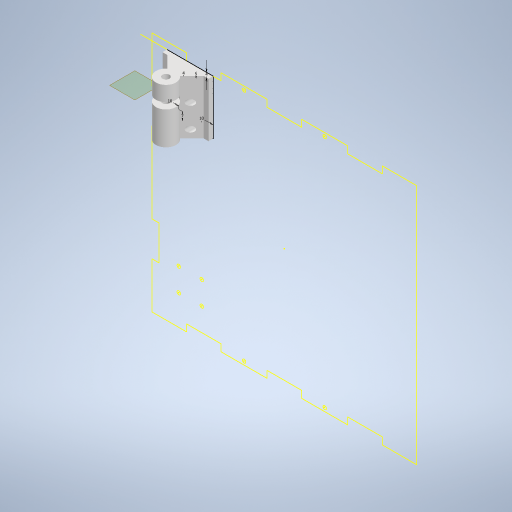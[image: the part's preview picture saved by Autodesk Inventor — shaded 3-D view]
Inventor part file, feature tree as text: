
AUTODESK INVENTOR PART (.ipt)
format: ipt  version: 2024.2 (Build 282272000, 272)  size: 331,776 bytes
history: native  units: mm
features: other x6, extrude x5, sketch x4, reference x3, chamfer x2
ambient origin geometry x8: Origin, YZ Plane, XZ Plane, XY Plane, X Axis, Y Axis, Z Axis, Center Point
bodies: Body1 (feature_tree)
feature tree (20):
  other  "Твердое тело1"
  sketch  "Эскиз1"
  extrude  "Выдавливание1"  Depth=10.0mm
  other  "РабПлоскость1"
  extrude  "Выдавливание3"  Depth=10.0mm
  extrude  "Выдавливание4"  Depth=7.0mm
  chamfer  "Фаска3"  Distance=4.0mm
  chamfer  "Фаска4"  Distance=5.0mm
  extrude  "Выдавливание5"  Depth=4.0mm
  extrude  "Выдавливание6"  Depth=4.0mm TaperAngle=0.0deg
  reference  "Ссылка1"
  reference  "Ссылка2"
  reference  "Ссылка3"
  sketch  "Эскиз2"
  sketch  "Эскиз3"
  sketch  "Эскиз4"
  other  "<userpath>\Documents\Artist-v2\3D\Робот.iam"
  other  "Робот.iam"
  other  "бок:1"
  other  "Низ робота:1"
